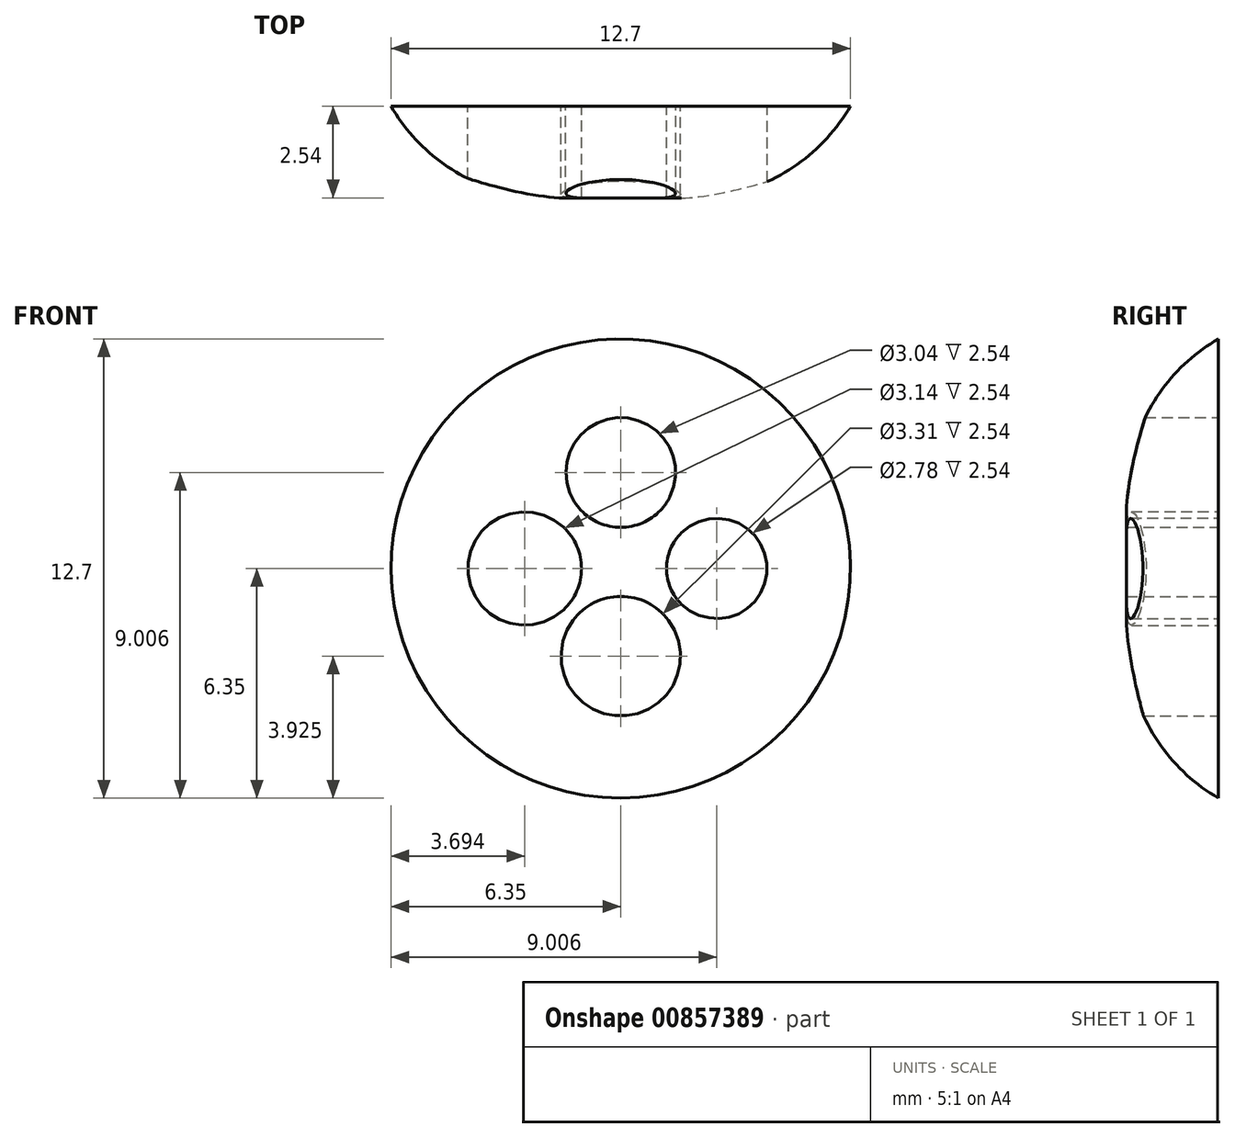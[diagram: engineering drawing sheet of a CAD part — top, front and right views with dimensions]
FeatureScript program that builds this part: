
annotation { "Feature Type Name" : "Feature", "Feature Type Description" : "" }
export const myFeature = defineFeature(function(context is Context, id is Id, definition is map)
    precondition{}
    {
        {
            var Q0;
            Q0=qCreatedBy(makeId("Front.planeOp"),FACE);
            var sketch = newSketch(context, id + "F0", { "sketchPlane" : qUnion([Q0])});
            skCircle(sketch, "E0", {"center": v(0, 0) * mm, "radius": 6.35 * mm});
            skCircle(sketch, "E1", {"center": v(0, 2.66) * mm, "radius": 1.52 * mm});
            skCircle(sketch, "E2", {"center": v(-2.66, 0) * mm, "radius": 1.57 * mm});
            skCircle(sketch, "E3", {"center": v(0, -2.43) * mm, "radius": 1.65 * mm});
            skCircle(sketch, "E4", {"center": v(2.66, 0) * mm, "radius": 1.4 * mm});
            skSolve(sketch);
        }
        {
            var Q0;
            Q0=makeQuery(id+"F0.imprint","IMPRINT",FACE,{"disambiguationData":[TD([[makeQuery(id+"F0.imprint","IMPRINT",EDGE,{"derivedFrom":sQuery(id+"F0.wireOp",EDGE,"E0")}),1.0]])]});
            extrude(context, id + "F1", {"entities" : qUnion([Q0]), "depth" : 2.54 * mm, "offsetDistance" : 25.4 * mm});
        }
        {
            var Q0;
            Q0=makeQuery(id+"F1.opExtrude","CAP_EDGE",EDGE,{"disambiguationData":[OSD([sQuery(id+"F0.wireOp",EDGE,"E0")])],"isStart":false});
            fillet(context, id + "F2", {"entities" : qUnion([Q0]), "radius" : 5.08 * mm, "tangentPropagation" : true, "allowEdgeOverflow" : false});
        }
    });
